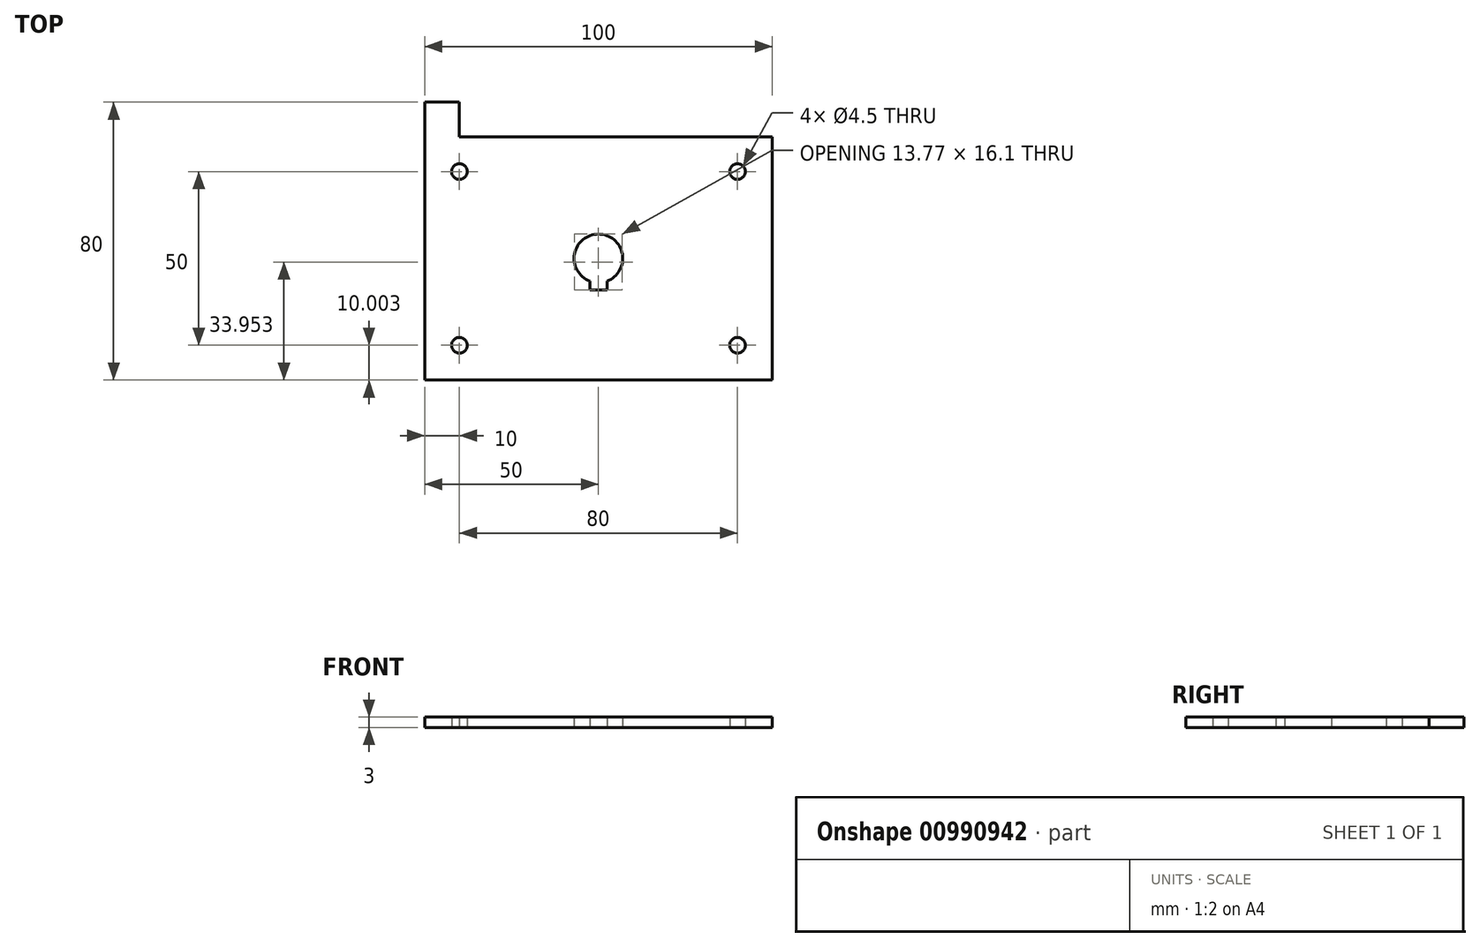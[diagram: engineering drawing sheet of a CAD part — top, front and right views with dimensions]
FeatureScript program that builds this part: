
annotation { "Feature Type Name" : "Feature", "Feature Type Description" : "" }
export const myFeature = defineFeature(function(context is Context, id is Id, definition is map)
    precondition{}
    {
        {
            var Q0;
            Q0=qCreatedBy(makeId("Top.planeOp"),FACE);
            var sketch = newSketch(context, id + "F0", { "sketchPlane" : qUnion([Q0])});
            skLineSegment(sketch, "E0", {"start": v(-2.5, -11.57) * mm, "end": v(-2.5, -14.13) * mm});
            skLineSegment(sketch, "E1", {"start": v(-2.5, -14.13) * mm, "end": v(2.5, -14.13) * mm});
            skLineSegment(sketch, "E2", {"start": v(2.5, -14.13) * mm, "end": v(2.5, -11.57) * mm});
            skCircle(sketch, "E3.converted", {"center": v(0, -5.03) * mm, "radius": 7 * mm});
            skPoint(sketch, "E4", {"position": v(0, -12.03) * mm});
            skLineSegment(sketch, "E5.bottom", {"start": v(50, -40.03) * mm, "end": v(-50, -40.03) * mm});
            skLineSegment(sketch, "E5.top", {"start": v(-40, 39.97) * mm, "end": v(-50, 39.97) * mm});
            skLineSegment(sketch, "E5.left", {"start": v(50, -40.03) * mm, "end": v(50, 29.97) * mm});
            skLineSegment(sketch, "E5.right", {"start": v(-50, -40.03) * mm, "end": v(-50, 39.97) * mm});
            skLineSegment(sketch, "E6", {"start": v(-50, 29.97) * mm, "end": v(50, 29.97) * mm});
            skLineSegment(sketch, "E7", {"start": v(-40, 39.97) * mm, "end": v(-40, 29.97) * mm});
            skPoint(sketch, "E8.orphan", {"position": v(50, 39.97) * mm});
            skLineSegment(sketch, "E9", {"start": v(-50, -40.03) * mm, "end": v(-50, 29.97) * mm});
            skPoint(sketch, "E10", {"position": v(-50, 19.97) * mm});
            skPoint(sketch, "E11", {"position": v(40, 19.97) * mm});
            skPoint(sketch, "E12", {"position": v(40, -30.03) * mm});
            skPoint(sketch, "E13", {"position": v(-50, -30.03) * mm});
            skCircle(sketch, "E14", {"center": v(40, 19.97) * mm, "radius": 2.25 * mm});
            skCircle(sketch, "E15.MirrorC", {"center": v(40, -30.03) * mm, "radius": 2.25 * mm});
            skCircle(sketch, "E16.MirrorC", {"center": v(-40, 19.97) * mm, "radius": 2.25 * mm});
            skCircle(sketch, "E17.MirrorC", {"center": v(-40, -30.03) * mm, "radius": 2.25 * mm});
            skSolve(sketch);
        }
        {
            var Q0;
            {var subQ7=sQuery(id+"F0.wireOp",EDGE,"E0");Q0=makeQuery(id+"F0.imprint","IMPRINT",FACE,{"disambiguationData":[TD([[makeQuery(id+"F0.imprint","IMPRINT",EDGE,{"derivedFrom":subQ7}),-1.0]])]});}
            var Q1;
            {var subQ5=sQuery(id+"F0.wireOp",EDGE,"4xxc5oVe-U1D8-RdDk-WCKI-GAU98GmUnVuJ");var subQ6=sQuery(id+"F0.wireOp",EDGE,"E5.bottom");var subQ7=makeQuery(id+"F0.imprint","INTERSECT",VERTEX,{"derivedFrom":[subQ6,subQ5]});Q1=makeQuery(id+"F0.imprint","IMPRINT",FACE,{"disambiguationData":[TD([[makeQuery(id+"F0.imprint","IMPRINT",EDGE,{"disambiguationData":[TD([[subQ7,-1.0]])],"derivedFrom":subQ6}),-1.0]])]});}
            var Q2;
            {var subQ5=sQuery(id+"F0.wireOp",EDGE,"4xxc5oVe-U1D8-RdDk-WCKI-GAU98GmUnVuJ");var subQ6=sQuery(id+"F0.wireOp",EDGE,"E5.bottom");var subQ7=makeQuery(id+"F0.imprint","INTERSECT",VERTEX,{"derivedFrom":[subQ6,subQ5]});Q2=makeQuery(id+"F0.imprint","IMPRINT",FACE,{"disambiguationData":[TD([[makeQuery(id+"F0.imprint","IMPRINT",EDGE,{"disambiguationData":[TD([[subQ7,1.0]])],"derivedFrom":subQ6}),-1.0]])]});}
            var Q3;
            {var subQ0=sQuery(id+"F0.wireOp",EDGE,"4jpTKrsM-aKTq-Esgq-MGsV-NbsFvEdi3Mff");var subQ5=sQuery(id+"F0.wireOp",EDGE,"E5.left");var subQ6=makeQuery(id+"F0.imprint","INTERSECT",VERTEX,{"derivedFrom":[subQ5,subQ0]});Q3=makeQuery(id+"F0.imprint","IMPRINT",FACE,{"disambiguationData":[TD([[makeQuery(id+"F0.imprint","IMPRINT",EDGE,{"disambiguationData":[TD([[subQ6,1.0]])],"derivedFrom":subQ5}),1.0]])]});}
            var Q4;
            {var subQ0=sQuery(id+"F0.wireOp",EDGE,"4jpTKrsM-aKTq-Esgq-MGsV-NbsFvEdi3Mff");var subQ1=sQuery(id+"F0.wireOp",EDGE,"E5.left");var subQ2=makeQuery(id+"F0.imprint","INTERSECT",VERTEX,{"derivedFrom":[subQ1,subQ0]});Q4=makeQuery(id+"F0.imprint","IMPRINT",FACE,{"disambiguationData":[TD([[makeQuery(id+"F0.imprint","IMPRINT",EDGE,{"disambiguationData":[TD([[subQ2,-1.0]])],"derivedFrom":subQ1}),1.0]])]});}
            var Q5;
            {var subQ1=sQuery(id+"F0.wireOp",EDGE,"E6");var subQ6=sQuery(id+"F0.wireOp",EDGE,"E5.left");var subQ9=makeQuery(id+"F0.imprint","INTERSECT",VERTEX,{"derivedFrom":[subQ6,subQ1]});Q5=makeQuery(id+"F0.imprint","IMPRINT",FACE,{"disambiguationData":[TD([[makeQuery(id+"F0.imprint","IMPRINT",EDGE,{"disambiguationData":[TD([[subQ9,1.0]])],"derivedFrom":subQ6}),1.0]])]});}
            var Q6;
            {var subQ1=sQuery(id+"F0.wireOp",EDGE,"FJSjo2PN-oite-CpyQ-YUBK-05txENasCkpn");var subQ8=sQuery(id+"F0.wireOp",EDGE,"E5.right");var subQ12=makeQuery(id+"F0.imprint","INTERSECT",VERTEX,{"derivedFrom":[subQ8,subQ1]});Q6=makeQuery(id+"F0.imprint","IMPRINT",FACE,{"disambiguationData":[TD([[makeQuery(id+"F0.imprint","IMPRINT",EDGE,{"disambiguationData":[TD([[subQ12,-1.0]])],"derivedFrom":subQ8}),-1.0]])]});}
            var Q7;
            {var subQ0=sQuery(id+"F0.wireOp",EDGE,"E5.top");Q7=makeQuery(id+"F0.imprint","IMPRINT",FACE,{"disambiguationData":[TD([[makeQuery(id+"F0.imprint","IMPRINT",EDGE,{"derivedFrom":subQ0}),1.0]])]});}
            extrude(context, id + "F1", {"entities" : qUnion([Q0, Q1, Q2, Q3, Q4, Q5, Q6, Q7]), "depth" : 3 * mm, "offsetDistance" : 25 * mm});
        }
    });
